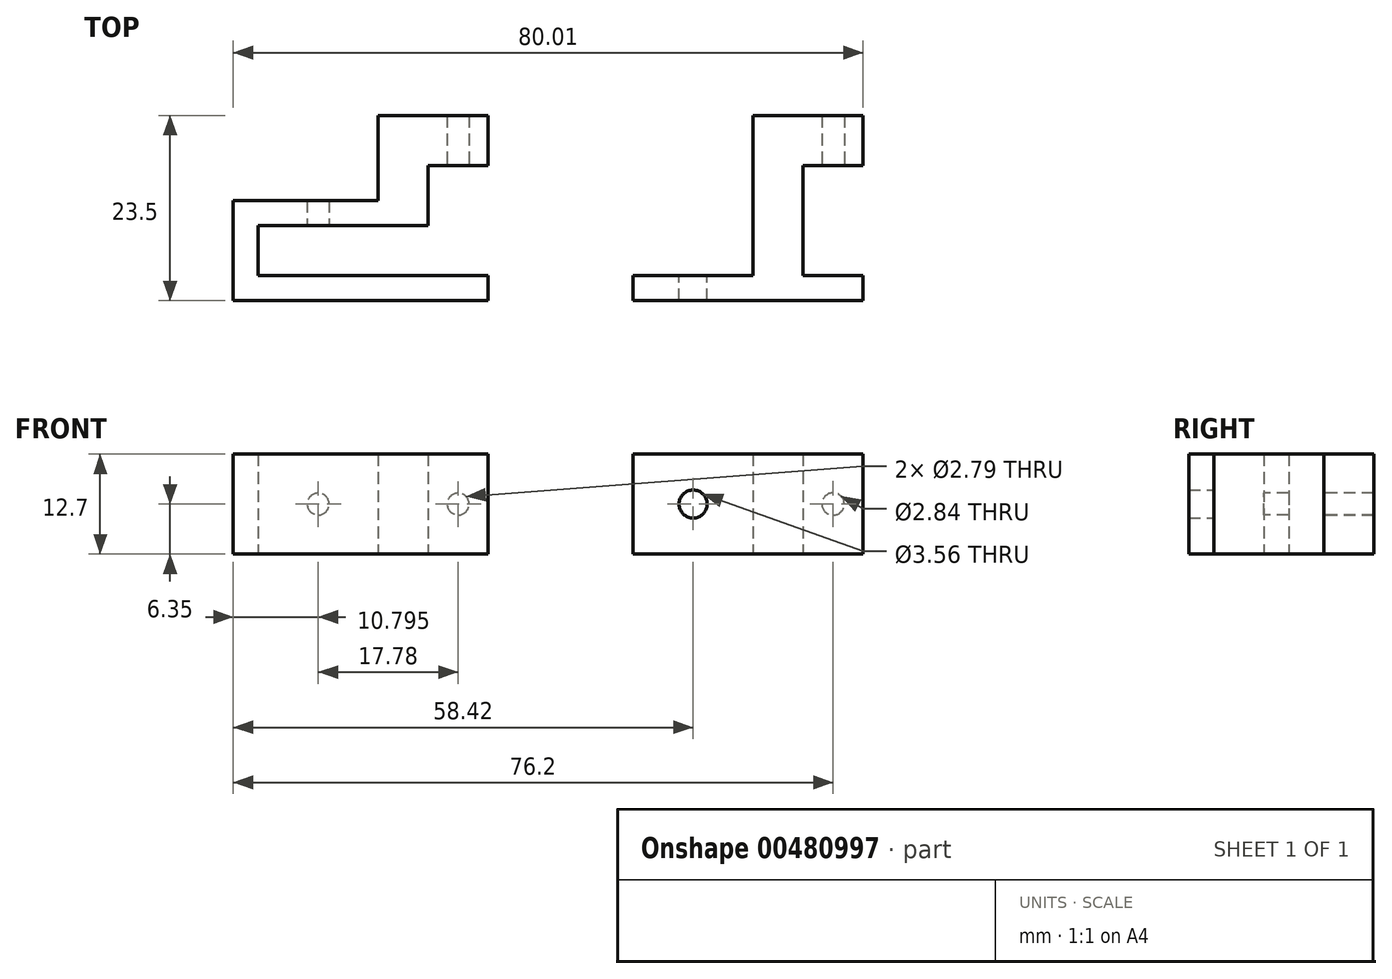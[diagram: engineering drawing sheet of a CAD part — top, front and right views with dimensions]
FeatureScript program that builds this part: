
annotation { "Feature Type Name" : "Feature", "Feature Type Description" : "" }
export const myFeature = defineFeature(function(context is Context, id is Id, definition is map)
    precondition{}
    {
        {
            var Q0;
            Q0=qCreatedBy(makeId("Top.planeOp"),FACE);
            var sketch = newSketch(context, id + "F0", { "sketchPlane" : qUnion([Q0])});
            skLineSegment(sketch, "E0", {"start": v(0, 0) * mm, "end": v(15.24, 0) * mm});
            skLineSegment(sketch, "E1", {"start": v(0, 0) * mm, "end": v(0, -3.17) * mm});
            skLineSegment(sketch, "E2", {"start": v(0, -3.17) * mm, "end": v(21.59, -3.17) * mm});
            skLineSegment(sketch, "E3", {"start": v(15.24, 0) * mm, "end": v(15.24, 20.32) * mm});
            skLineSegment(sketch, "E4", {"start": v(15.24, 20.32) * mm, "end": v(29.21, 20.32) * mm});
            skLineSegment(sketch, "E5", {"start": v(29.2, 20.32) * mm, "end": v(29.2, 13.97) * mm});
            skLineSegment(sketch, "E6", {"start": v(29.21, 13.97) * mm, "end": v(21.59, 13.97) * mm});
            skLineSegment(sketch, "E7", {"start": v(21.6, 13.97) * mm, "end": v(21.6, 0) * mm});
            skLineSegment(sketch, "E8", {"start": v(21.6, 0) * mm, "end": v(29.21, 0) * mm});
            skLineSegment(sketch, "E9", {"start": v(29.21, 0) * mm, "end": v(29.21, -3.18) * mm});
            skLineSegment(sketch, "E10", {"start": v(29.21, -3.18) * mm, "end": v(21.59, -3.18) * mm});
            skSolve(sketch);
        }
        {
            var Q0;
            Q0 = qSketchRegion(id + "F0", true);
            extrude(context, id + "F1", {"entities" : qUnion([Q0]), "depth" : 12.7 * mm});
        }
        {
            var Q0;
            Q0=makeQuery(id+"F1.opExtrude","SWEPT_FACE",FACE,{"disambiguationData":[OSD([sQuery(id+"F0.wireOp",EDGE,"E6")])]});
            var sketch = newSketch(context, id + "F2", { "sketchPlane" : qUnion([Q0])});
            skLineSegment(sketch, "E11.0.0", {"start": v(21.6, 0) * mm, "end": v(29.21, 0) * mm});
            skLineSegment(sketch, "E11.0.1", {"start": v(29.21, 0) * mm, "end": v(29.21, 12.7) * mm});
            skLineSegment(sketch, "E11.0.2", {"start": v(29.21, 12.7) * mm, "end": v(21.6, 12.7) * mm});
            skLineSegment(sketch, "E11.0.3", {"start": v(21.6, 12.7) * mm, "end": v(21.6, 0) * mm});
            skCircle(sketch, "E12", {"center": v(25.4, 6.35) * mm, "radius": 1.42 * mm});
            skPoint(sketch, "E12.centerSnap0", {"position": v(25.4, 12.7) * mm});
            skPoint(sketch, "E12.centerSnap1", {"position": v(29.21, 6.35) * mm});
            skSolve(sketch);
        }
        {
            var Q0;
            Q0=makeQuery(id+"F2.imprint","IMPRINT",FACE,{"disambiguationData":[TD([[makeQuery(id+"F2.imprint","IMPRINT",EDGE,{"derivedFrom":sQuery(id+"F2.wireOp",EDGE,"E12")}),1.0]])]});
            extrude(context, id + "F3", {"entities" : qUnion([Q0]), "operationType" : NewBodyOperationType.REMOVE, "oppositeDirection" : true, "depth" : 25.4 * mm});
        }
        {
            var Q0;
            Q0=makeQuery(id+"F1.opExtrude","SWEPT_FACE",FACE,{"disambiguationData":[OSD([sQuery(id+"F0.wireOp",EDGE,"E0")])]});
            var sketch = newSketch(context, id + "F4", { "sketchPlane" : qUnion([Q0])});
            skLineSegment(sketch, "E13.0.0", {"start": v(-15.24, 0) * mm, "end": v(0, 0) * mm});
            skLineSegment(sketch, "E13.0.1", {"start": v(0, 0) * mm, "end": v(0, 12.7) * mm});
            skLineSegment(sketch, "E13.0.2", {"start": v(0, 12.7) * mm, "end": v(-15.24, 12.7) * mm});
            skLineSegment(sketch, "E13.0.3", {"start": v(-15.24, 12.7) * mm, "end": v(-15.24, 0) * mm});
            skCircle(sketch, "E14", {"center": v(-7.62, 6.35) * mm, "radius": 1.78 * mm});
            skPoint(sketch, "E14.centerSnap0", {"position": v(-7.62, 12.7) * mm});
            skPoint(sketch, "E14.centerSnap1", {"position": v(0, 6.35) * mm});
            skSolve(sketch);
        }
        {
            var Q0;
            Q0=makeQuery(id+"F4.imprint","IMPRINT",FACE,{"disambiguationData":[TD([[makeQuery(id+"F4.imprint","IMPRINT",EDGE,{"derivedFrom":sQuery(id+"F4.wireOp",EDGE,"E14")}),1.0]])]});
            extrude(context, id + "F5", {"entities" : qUnion([Q0]), "operationType" : NewBodyOperationType.REMOVE, "oppositeDirection" : true, "depth" : 25.4 * mm});
        }
        {
            var Q0;
            Q0=qCreatedBy(makeId("Top.planeOp"),FACE);
            var sketch = newSketch(context, id + "F6", { "sketchPlane" : qUnion([Q0])});
            skLineSegment(sketch, "E15", {"start": v(-47.63, 0) * mm, "end": v(-47.63, 6.35) * mm});
            skLineSegment(sketch, "E16", {"start": v(-47.63, 6.35) * mm, "end": v(-32.39, 6.35) * mm});
            skLineSegment(sketch, "E17", {"start": v(-47.63, 0) * mm, "end": v(-32.39, 0) * mm});
            skLineSegment(sketch, "E18", {"start": v(-32.39, -3.17) * mm, "end": v(-47.63, -3.18) * mm});
            skLineSegment(sketch, "E19", {"start": v(-47.63, -3.18) * mm, "end": v(-50.8, -3.18) * mm});
            skLineSegment(sketch, "E20", {"start": v(-50.8, -3.18) * mm, "end": v(-50.8, 9.53) * mm});
            skLineSegment(sketch, "E21", {"start": v(-50.8, 9.53) * mm, "end": v(-47.63, 9.53) * mm});
            skLineSegment(sketch, "E22", {"start": v(-47.63, 9.53) * mm, "end": v(-32.39, 9.53) * mm});
            skLineSegment(sketch, "E23", {"start": v(-32.39, 9.53) * mm, "end": v(-32.39, 20.32) * mm});
            skLineSegment(sketch, "E24", {"start": v(-32.39, 20.32) * mm, "end": v(-18.42, 20.32) * mm});
            skLineSegment(sketch, "E25", {"start": v(-18.42, 20.32) * mm, "end": v(-18.42, 13.97) * mm});
            skLineSegment(sketch, "E26", {"start": v(-18.42, 13.97) * mm, "end": v(-26.04, 13.97) * mm});
            skLineSegment(sketch, "E27", {"start": v(-26.04, 13.97) * mm, "end": v(-26.04, 6.35) * mm});
            skLineSegment(sketch, "E28", {"start": v(-26.04, 6.35) * mm, "end": v(-32.39, 6.35) * mm});
            skLineSegment(sketch, "E29", {"start": v(-32.39, 0) * mm, "end": v(-18.42, 0) * mm});
            skLineSegment(sketch, "E30", {"start": v(-18.42, 0) * mm, "end": v(-18.42, -3.17) * mm});
            skLineSegment(sketch, "E31", {"start": v(-18.42, -3.17) * mm, "end": v(-32.39, -3.17) * mm});
            skLineSegment(sketch, "E32.0.0", {"start": v(0, -3.18) * mm, "end": v(29.21, -3.18) * mm});
            skLineSegment(sketch, "E32.0.1", {"start": v(29.21, -3.18) * mm, "end": v(29.21, 0) * mm});
            skLineSegment(sketch, "E32.0.2", {"start": v(29.21, 0) * mm, "end": v(21.6, 0) * mm});
            skLineSegment(sketch, "E32.0.3", {"start": v(21.6, 0) * mm, "end": v(21.6, 13.97) * mm});
            skLineSegment(sketch, "E32.0.4", {"start": v(21.59, 13.97) * mm, "end": v(29.2, 13.97) * mm});
            skLineSegment(sketch, "E32.0.5", {"start": v(29.2, 13.97) * mm, "end": v(29.2, 20.32) * mm});
            skLineSegment(sketch, "E32.0.6", {"start": v(29.21, 20.32) * mm, "end": v(15.24, 20.32) * mm});
            skLineSegment(sketch, "E32.0.7", {"start": v(15.24, 20.32) * mm, "end": v(15.24, 0) * mm});
            skLineSegment(sketch, "E32.0.8", {"start": v(15.24, 0) * mm, "end": v(0, 0) * mm});
            skLineSegment(sketch, "E32.0.9", {"start": v(0, 0) * mm, "end": v(0, -3.17) * mm});
            skSolve(sketch);
        }
        {
            var Q0;
            Q0=makeQuery(id+"F6.imprint","IMPRINT",FACE,{"disambiguationData":[TD([[makeQuery(id+"F6.imprint","IMPRINT",EDGE,{"derivedFrom":sQuery(id+"F6.wireOp",EDGE,"E15")}),1.0]])]});
            extrude(context, id + "F7", {"entities" : qUnion([Q0]), "depth" : 12.7 * mm});
        }
        {
            var Q0;
            Q0=makeQuery(id+"F7.opExtrude","SWEPT_FACE",FACE,{"disambiguationData":[OSD([sQuery(id+"F6.wireOp",EDGE,"E26")])]});
            var sketch = newSketch(context, id + "F8", { "sketchPlane" : qUnion([Q0])});
            skLineSegment(sketch, "E33.0.0", {"start": v(-26.04, 0) * mm, "end": v(-18.42, 0) * mm});
            skLineSegment(sketch, "E33.0.1", {"start": v(-18.42, 0) * mm, "end": v(-18.42, 12.7) * mm});
            skLineSegment(sketch, "E33.0.2", {"start": v(-18.42, 12.7) * mm, "end": v(-26.04, 12.7) * mm});
            skLineSegment(sketch, "E33.0.3", {"start": v(-26.04, 12.7) * mm, "end": v(-26.04, 0) * mm});
            skCircle(sketch, "E34", {"center": v(-22.23, 6.35) * mm, "radius": 1.4 * mm});
            skPoint(sketch, "E34.centerSnap0", {"position": v(-22.23, 12.7) * mm});
            skPoint(sketch, "E34.centerSnap1", {"position": v(-18.42, 6.35) * mm});
            skSolve(sketch);
        }
        {
            var Q0;
            Q0=makeQuery(id+"F8.imprint","IMPRINT",FACE,{"disambiguationData":[TD([[makeQuery(id+"F8.imprint","IMPRINT",EDGE,{"derivedFrom":sQuery(id+"F8.wireOp",EDGE,"E34")}),1.0]])]});
            extrude(context, id + "F9", {"entities" : qUnion([Q0]), "operationType" : NewBodyOperationType.REMOVE, "oppositeDirection" : true, "depth" : 25.4 * mm});
        }
        {
            var Q0;
            Q0=makeQuery(id+"F7.opExtrude","SWEPT_FACE",FACE,{"disambiguationData":[OSD([sQuery(id+"F6.wireOp",EDGE,"E16"),sQuery(id+"F6.wireOp",EDGE,"E28")])]});
            var sketch = newSketch(context, id + "F10", { "sketchPlane" : qUnion([Q0])});
            skLineSegment(sketch, "E35.0", {"start": v(-50.8, 12.7) * mm, "end": v(-32.39, 12.7) * mm});
            skPoint(sketch, "E36.0", {"position": v(-47.63, 12.7) * mm});
            skLineSegment(sketch, "E37", {"start": v(-47.63, 12.7) * mm, "end": v(-32.39, 12.7) * mm});
            skLineSegment(sketch, "E38", {"start": v(-32.39, 12.7) * mm, "end": v(-32.39, 0) * mm});
            skPoint(sketch, "E38.endSnap0", {"position": v(-36.83, 0) * mm});
            skCircle(sketch, "E39", {"center": v(-40, 6.35) * mm, "radius": 1.4 * mm});
            skPoint(sketch, "E39.centerSnap0", {"position": v(-40, 12.7) * mm});
            skPoint(sketch, "E39.centerSnap1", {"position": v(-32.39, 6.35) * mm});
            skSolve(sketch);
        }
        {
            var Q0;
            Q0 = qSketchRegion(id + "F10", true);
            extrude(context, id + "F11", {"entities" : qUnion([Q0]), "operationType" : NewBodyOperationType.REMOVE, "oppositeDirection" : true, "depth" : 25.4 * mm});
        }
    });
